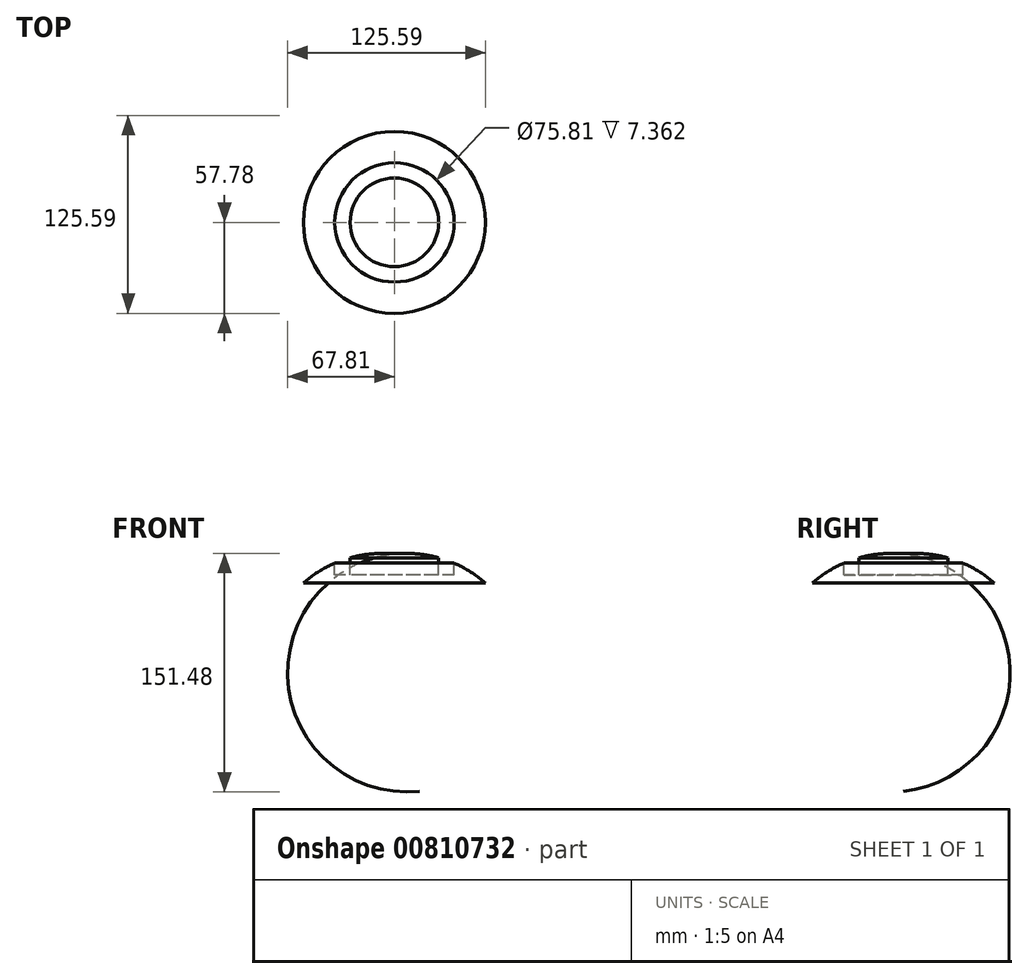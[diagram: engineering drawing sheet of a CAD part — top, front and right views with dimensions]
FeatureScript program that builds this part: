
annotation { "Feature Type Name" : "Feature", "Feature Type Description" : "" }
export const myFeature = defineFeature(function(context is Context, id is Id, definition is map)
    precondition{}
    {
        {
            var Q0;
            Q0=qCreatedBy(makeId("Front.planeOp"),FACE);
            var sketch = newSketch(context, id + "F0", { "sketchPlane" : qUnion([Q0])});
            skArc(sketch, "E0", {"start": v(57.78, 0) * mm, "mid": v(30.8, 15.19) * mm, "end": v(0, 18.3) * mm});
            skLineSegment(sketch, "E1", {"start": v(0, 18.3) * mm, "end": v(0, 0) * mm});
            skLineSegment(sketch, "E2", {"start": v(0, 0) * mm, "end": v(57.78, 0) * mm});
            skLineSegment(sketch, "E3", {"start": v(28.16, 15.97) * mm, "end": v(28.16, 5.18) * mm});
            skLineSegment(sketch, "E4", {"start": v(28.16, 5.18) * mm, "end": v(37.9, 5.18) * mm});
            skLineSegment(sketch, "E5", {"start": v(37.9, 5.18) * mm, "end": v(37.9, 12.54) * mm});
            skSolve(sketch);
        }
        {
            var Q0;
            {var subQ1=sQuery(id+"F0.wireOp",EDGE,"E1");Q0=makeQuery(id+"F0.imprint","IMPRINT",FACE,{"disambiguationData":[TD([[makeQuery(id+"F0.imprint","IMPRINT",EDGE,{"derivedFrom":subQ1}),1.0]])]});}
            var Q1;
            Q1=sQuery(id+"F0.wireOp",EDGE,"E1");
            revolve(context, id + "F1", {"surfaceOperationType" : NewSurfaceOperationType.NEW, "entities" : qUnion([Q0]), "axis" : qUnion([Q1]), "revolveType" : RevolveType.FULL});
        }
    });
